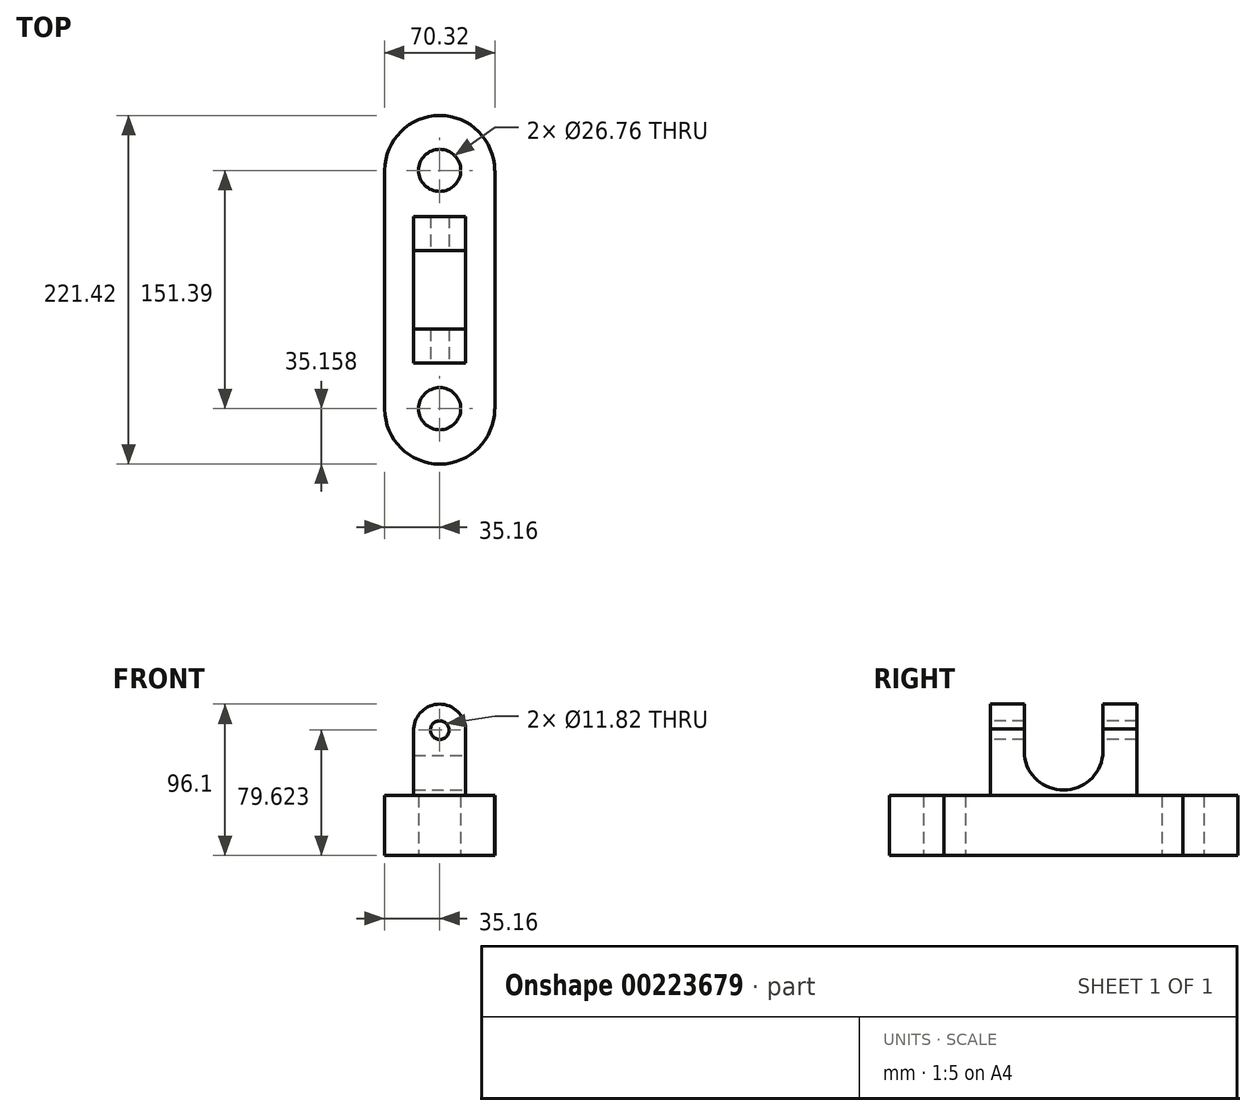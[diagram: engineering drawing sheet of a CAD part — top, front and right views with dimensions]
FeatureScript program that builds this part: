
annotation { "Feature Type Name" : "Feature", "Feature Type Description" : "" }
export const myFeature = defineFeature(function(context is Context, id is Id, definition is map)
    precondition{}
    {
        {
            var Q0;
            Q0=qCreatedBy(makeId("Top.planeOp"),FACE);
            var sketch = newSketch(context, id + "F0", { "sketchPlane" : qUnion([Q0])});
            skLineSegment(sketch, "E0.bottom", {"start": v(-35.16, 75.84) * mm, "end": v(-34.88, 75.84) * mm});
            skLineSegment(sketch, "E0.top", {"start": v(-35.16, -75.84) * mm, "end": v(-34.88, -75.84) * mm});
            skLineSegment(sketch, "E0.left", {"start": v(-35.16, 75.84) * mm, "end": v(-35.16, -75.84) * mm});
            skLineSegment(sketch, "E0.right", {"start": v(35.16, 75.84) * mm, "end": v(35.16, -75.84) * mm});
            skPoint(sketch, "E0.middle", {"position": v(0, 0) * mm});
            skArc(sketch, "E1", {"start": v(34.88, 75.84) * mm, "mid": v(0, 110.71) * mm, "end": v(-34.88, 75.84) * mm});
            skArc(sketch, "E2", {"start": v(-34.88, -75.84) * mm, "mid": v(0, -110.71) * mm, "end": v(34.88, -75.84) * mm});
            skLineSegment(sketch, "E3.trimOffspring", {"start": v(34.88, 75.84) * mm, "end": v(35.16, 75.84) * mm});
            skLineSegment(sketch, "E4.trimOffspring", {"start": v(34.88, -75.84) * mm, "end": v(35.16, -75.84) * mm});
            skCircle(sketch, "E5", {"center": v(0, 75.84) * mm, "radius": 13.38 * mm});
            skCircle(sketch, "E6", {"center": v(0, -75.55) * mm, "radius": 13.38 * mm});
            skSolve(sketch);
        }
        {
            var Q0;
            Q0 = qSketchRegion(id + "F0", true);
            extrude(context, id + "F1", {"entities" : qUnion([Q0]), "depth" : 38.1 * mm});
        }
        {
            var Q0;
            Q0=makeQuery(id+"F1.opExtrude","CAP_FACE",FACE,{"disambiguationData":[OSD([sQuery(id+"F0.wireOp",EDGE,"E0.bottom"),sQuery(id+"F0.wireOp",EDGE,"E0.top"),sQuery(id+"F0.wireOp",EDGE,"E0.left"),sQuery(id+"F0.wireOp",EDGE,"E0.right"),sQuery(id+"F0.wireOp",EDGE,"E1"),sQuery(id+"F0.wireOp",EDGE,"E2"),sQuery(id+"F0.wireOp",EDGE,"E3.trimOffspring"),sQuery(id+"F0.wireOp",EDGE,"E4.trimOffspring"),sQuery(id+"F0.wireOp",EDGE,"E5"),sQuery(id+"F0.wireOp",EDGE,"E6")])],"isStart":false});
            var sketch = newSketch(context, id + "F2", { "sketchPlane" : qUnion([Q0])});
            skLineSegment(sketch, "E7.bottom", {"start": v(-16.45, 46.54) * mm, "end": v(16.45, 46.54) * mm});
            skLineSegment(sketch, "E7.top", {"start": v(-16.45, -46.54) * mm, "end": v(16.45, -46.54) * mm});
            skLineSegment(sketch, "E7.left", {"start": v(-16.45, 46.54) * mm, "end": v(-16.45, -46.54) * mm});
            skLineSegment(sketch, "E7.right", {"start": v(16.45, 46.54) * mm, "end": v(16.45, -46.54) * mm});
            skPoint(sketch, "E7.middle", {"position": v(0, 0) * mm});
            skSolve(sketch);
        }
        {
            var Q0;
            Q0 = qSketchRegion(id + "F2", true);
            extrude(context, id + "F3", {"entities" : qUnion([Q0]), "operationType" : NewBodyOperationType.ADD, "depth" : 63.5 * mm});
        }
        {
            var Q0;
            Q0=makeQuery(id+"F3.opExtrude","SWEPT_FACE",FACE,{"disambiguationData":[OSD([sQuery(id+"F2.wireOp",EDGE,"E7.top")])]});
            var sketch = newSketch(context, id + "F4", { "sketchPlane" : qUnion([Q0])});
            skArc(sketch, "E8", {"start": v(16.45, 78.82) * mm, "mid": v(0, 96.1) * mm, "end": v(-16.45, 78.82) * mm});
            skPoint(sketch, "E8.centerSnap0", {"position": v(0, 101.6) * mm});
            skCircle(sketch, "E9", {"center": v(0, 79.62) * mm, "radius": 5.91 * mm});
            skSolve(sketch);
        }
        {
            var Q0;
            {var subQ1=sQuery(id+"F2.wireOp",EDGE,"E7.top");var subQ6=makeQuery(id+"F3.opExtrude","CAP_EDGE",EDGE,{"disambiguationData":[OSD([subQ1])],"isStart":false});Q0=makeQuery(id+"F4.imprint","IMPRINT",FACE,{"disambiguationData":[TD([[makeQuery(id+"F4.imprint","IMPRINT",EDGE,{"derivedFrom":subQ6}),-1.0]])]});}
            var Q1;
            Q1=makeQuery(id+"F4.imprint","IMPRINT",FACE,{"disambiguationData":[TD([[makeQuery(id+"F4.imprint","IMPRINT",EDGE,{"derivedFrom":sQuery(id+"F4.wireOp",EDGE,"E9")}),1.0]])]});
            extrude(context, id + "F5", {"entities" : qUnion([Q0, Q1]), "operationType" : NewBodyOperationType.REMOVE, "endBound" : BoundingType.THROUGH_ALL, "oppositeDirection" : true, "depth" : 25.4 * mm});
        }
        {
            var Q0;
            Q0=makeQuery(id+"F3.opExtrude","SWEPT_FACE",FACE,{"disambiguationData":[OSD([sQuery(id+"F2.wireOp",EDGE,"E7.right")])]});
            var sketch = newSketch(context, id + "F6", { "sketchPlane" : qUnion([Q0])});
            skLineSegment(sketch, "E10.top", {"start": v(-24.93, 112.01) * mm, "end": v(24.93, 112.01) * mm});
            skLineSegment(sketch, "E10.left", {"start": v(-24.93, 63.48) * mm, "end": v(-24.93, 112.01) * mm});
            skLineSegment(sketch, "E10.right", {"start": v(24.93, 63.48) * mm, "end": v(24.93, 112.01) * mm});
            skPoint(sketch, "E10.middle", {"position": v(0, 80.43) * mm});
            skArc(sketch, "E11", {"start": v(-24.93, 63.48) * mm, "mid": v(0, 41.54) * mm, "end": v(24.93, 63.48) * mm});
            skPoint(sketch, "E12.orphan", {"position": v(-24.93, 48.85) * mm});
            skPoint(sketch, "E10.bottom.end.orphan", {"position": v(24.93, 48.85) * mm});
            skSolve(sketch);
        }
        {
            var Q0;
            {var subQ0=sQuery(id+"F6.wireOp",EDGE,"E11");Q0=makeQuery(id+"F6.imprint","IMPRINT",FACE,{"disambiguationData":[TD([[makeQuery(id+"F6.imprint","IMPRINT",EDGE,{"derivedFrom":subQ0}),1.0]])]});}
            var Q1;
            {var subQ0=sQuery(id+"F6.wireOp",EDGE,"E10.top");Q1=makeQuery(id+"F6.imprint","IMPRINT",FACE,{"disambiguationData":[TD([[makeQuery(id+"F6.imprint","IMPRINT",EDGE,{"derivedFrom":subQ0}),-1.0]])]});}
            extrude(context, id + "F7", {"entities" : qUnion([Q0, Q1]), "operationType" : NewBodyOperationType.REMOVE, "endBound" : BoundingType.THROUGH_ALL, "oppositeDirection" : true, "depth" : 25.4 * mm});
        }
    });
